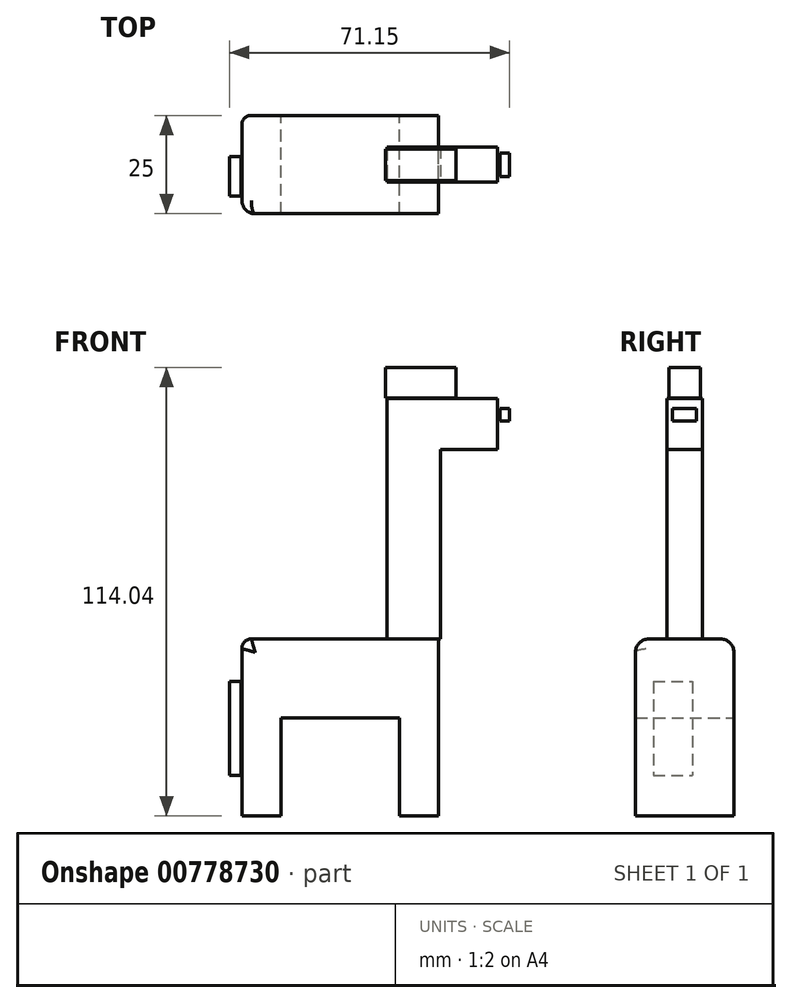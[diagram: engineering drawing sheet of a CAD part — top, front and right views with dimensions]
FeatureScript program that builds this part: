
annotation { "Feature Type Name" : "Feature", "Feature Type Description" : "" }
export const myFeature = defineFeature(function(context is Context, id is Id, definition is map)
    precondition{}
    {
        {
            var Q0;
            Q0=qCreatedBy(makeId("Front.planeOp"),FACE);
            var sketch = newSketch(context, id + "F0", { "sketchPlane" : qUnion([Q0])});
            skLineSegment(sketch, "E0.bottom", {"start": v(-30.99, 0) * mm, "end": v(-20.99, 0) * mm});
            skLineSegment(sketch, "E0.top", {"start": v(-30.99, 25) * mm, "end": v(-20.99, 25) * mm});
            skLineSegment(sketch, "E0.left", {"start": v(-30.99, 0) * mm, "end": v(-30.99, 25) * mm});
            skLineSegment(sketch, "E0.right", {"start": v(-20.99, 0) * mm, "end": v(-20.99, 25) * mm});
            skLineSegment(sketch, "E1.bottom", {"start": v(9.01, 0) * mm, "end": v(19.01, 0) * mm});
            skLineSegment(sketch, "E1.top", {"start": v(9.01, 25) * mm, "end": v(19.01, 25) * mm});
            skLineSegment(sketch, "E1.left", {"start": v(9.01, 0) * mm, "end": v(9.01, 25) * mm});
            skLineSegment(sketch, "E1.right", {"start": v(19.01, 0) * mm, "end": v(19.01, 25) * mm});
            skLineSegment(sketch, "E2.bottom", {"start": v(-30.99, 25) * mm, "end": v(19.01, 25) * mm});
            skLineSegment(sketch, "E2.top", {"start": v(-30.99, 45) * mm, "end": v(19.01, 45) * mm});
            skLineSegment(sketch, "E2.left", {"start": v(-30.99, 25) * mm, "end": v(-30.99, 45) * mm});
            skLineSegment(sketch, "E2.right", {"start": v(19.01, 25) * mm, "end": v(19.01, 45) * mm});
            skSolve(sketch);
        }
        {
            var Q0;
            Q0=makeQuery(id+"F0.imprint","IMPRINT",FACE,{"disambiguationData":[TD([[makeQuery(id+"F0.imprint","IMPRINT",EDGE,{"derivedFrom":sQuery(id+"F0.wireOp",EDGE,"E2.top")}),-1.0]])]});
            var Q1;
            Q1=makeQuery(id+"F0.imprint","IMPRINT",FACE,{"disambiguationData":[TD([[makeQuery(id+"F0.imprint","IMPRINT",EDGE,{"derivedFrom":sQuery(id+"F0.wireOp",EDGE,"E1.bottom")}),1.0]])]});
            var Q2;
            Q2=makeQuery(id+"F0.imprint","IMPRINT",FACE,{"disambiguationData":[TD([[makeQuery(id+"F0.imprint","IMPRINT",EDGE,{"derivedFrom":sQuery(id+"F0.wireOp",EDGE,"E0.bottom")}),1.0]])]});
            extrude(context, id + "F1", {"entities" : qUnion([Q0, Q1, Q2]), "endBound" : BoundingType.SYMMETRIC, "depth" : 25 * mm, "offsetDistance" : 25 * mm});
        }
        {
            var Q0;
            Q0=qCreatedBy(makeId("Front.planeOp"),FACE);
            var sketch = newSketch(context, id + "F2", { "sketchPlane" : qUnion([Q0])});
            skLineSegment(sketch, "E3.bottom", {"start": v(19.5, 45.05) * mm, "end": v(5.9, 45.05) * mm});
            skLineSegment(sketch, "E3.top", {"start": v(19.5, 93.12) * mm, "end": v(5.9, 93.12) * mm});
            skLineSegment(sketch, "E3.left", {"start": v(19.5, 45.05) * mm, "end": v(19.5, 93.12) * mm});
            skLineSegment(sketch, "E3.right", {"start": v(5.9, 45.05) * mm, "end": v(5.9, 93.12) * mm});
            skLineSegment(sketch, "E4.bottom", {"start": v(5.9, 106.11) * mm, "end": v(34.01, 106.11) * mm});
            skLineSegment(sketch, "E4.top", {"start": v(5.9, 93.12) * mm, "end": v(34.01, 93.12) * mm});
            skLineSegment(sketch, "E4.left", {"start": v(5.9, 106.11) * mm, "end": v(5.9, 93.12) * mm});
            skLineSegment(sketch, "E4.right", {"start": v(34.01, 106.11) * mm, "end": v(34.01, 93.12) * mm});
            skSolve(sketch);
        }
        {
            var Q0;
            Q0=makeQuery(id+"F2.imprint","IMPRINT",FACE,{"disambiguationData":[TD([[makeQuery(id+"F2.imprint","IMPRINT",EDGE,{"derivedFrom":sQuery(id+"F2.wireOp",EDGE,"E4.bottom")}),-1.0]])]});
            var Q1;
            Q1 = qSketchRegion(id + "F2", true);
            extrude(context, id + "F3", {"entities" : qUnion([Q0, Q1]), "endBound" : BoundingType.SYMMETRIC, "oppositeDirection" : true, "depth" : 9 * mm, "offsetDistance" : 25 * mm});
        }
        {
            var Q0;
            Q0=qCreatedBy(makeId("Front.planeOp"),FACE);
            var sketch = newSketch(context, id + "F4", { "sketchPlane" : qUnion([Q0])});
            skLineSegment(sketch, "E5.bottom", {"start": v(34.24, 99.53) * mm, "end": v(36.6, 99.53) * mm});
            skLineSegment(sketch, "E5.top", {"start": v(34.24, 96.5) * mm, "end": v(36.6, 96.5) * mm});
            skLineSegment(sketch, "E5.left", {"start": v(34.24, 99.53) * mm, "end": v(34.24, 96.5) * mm});
            skLineSegment(sketch, "E5.right", {"start": v(36.6, 99.53) * mm, "end": v(36.6, 96.5) * mm});
            skLineSegment(sketch, "E6.bottom", {"start": v(-31.55, 38.8) * mm, "end": v(-35.26, 38.8) * mm});
            skLineSegment(sketch, "E6.top", {"start": v(-31.55, 14.84) * mm, "end": v(-35.26, 14.84) * mm});
            skLineSegment(sketch, "E6.left", {"start": v(-31.55, 38.8) * mm, "end": v(-31.55, 14.84) * mm});
            skLineSegment(sketch, "E6.right", {"start": v(-35.26, 38.8) * mm, "end": v(-35.26, 14.84) * mm});
            skLineSegment(sketch, "E7.bottom", {"start": v(23.45, 106.28) * mm, "end": v(5.57, 106.28) * mm});
            skLineSegment(sketch, "E7.top", {"start": v(23.45, 114.04) * mm, "end": v(5.57, 114.04) * mm});
            skLineSegment(sketch, "E7.left", {"start": v(23.45, 106.28) * mm, "end": v(23.45, 114.04) * mm});
            skLineSegment(sketch, "E7.right", {"start": v(5.57, 106.28) * mm, "end": v(5.57, 114.04) * mm});
            skSolve(sketch);
        }
        {
            var Q0;
            Q0=makeQuery(id+"F4.imprint","IMPRINT",FACE,{"disambiguationData":[TD([[makeQuery(id+"F4.imprint","IMPRINT",EDGE,{"derivedFrom":sQuery(id+"F4.wireOp",EDGE,"E7.bottom")}),-1.0]])]});
            extrude(context, id + "F5", {"entities" : qUnion([Q0]), "endBound" : BoundingType.SYMMETRIC, "depth" : 8 * mm, "offsetDistance" : 25 * mm});
        }
        {
            var Q0;
            Q0=qCreatedBy(makeId("Front.planeOp"),FACE);
            var sketch = newSketch(context, id + "F6", { "sketchPlane" : qUnion([Q0])});
            skLineSegment(sketch, "E8.bottom", {"start": v(34.56, 99.45) * mm, "end": v(37.02, 99.45) * mm});
            skLineSegment(sketch, "E8.top", {"start": v(34.56, 96.26) * mm, "end": v(37.02, 96.26) * mm});
            skLineSegment(sketch, "E8.left", {"start": v(34.56, 99.45) * mm, "end": v(34.56, 96.26) * mm});
            skLineSegment(sketch, "E8.right", {"start": v(37.02, 99.45) * mm, "end": v(37.02, 96.26) * mm});
            skSolve(sketch);
        }
        {
            var Q0;
            Q0=makeQuery(id+"F6.imprint","IMPRINT",FACE,{"disambiguationData":[TD([[makeQuery(id+"F6.imprint","IMPRINT",EDGE,{"derivedFrom":sQuery(id+"F6.wireOp",EDGE,"E8.bottom")}),-1.0]])]});
            extrude(context, id + "F7", {"entities" : qUnion([Q0]), "endBound" : BoundingType.SYMMETRIC, "depth" : 6 * mm, "offsetDistance" : 25 * mm});
        }
        {
            var Q0;
            Q0=makeQuery(id+"F1.opExtrude","CAP_EDGE",EDGE,{"disambiguationData":[OSD([sQuery(id+"F0.wireOp",EDGE,"E2.top")])],"isStart":false});
            var Q1;
            Q1=makeQuery(id+"F1.opExtrude","CAP_EDGE",EDGE,{"disambiguationData":[OSD([sQuery(id+"F0.wireOp",EDGE,"E0.left"),sQuery(id+"F0.wireOp",EDGE,"E2.left")])],"isStart":false});
            fillet(context, id + "F8", {"entities" : qUnion([Q0, Q1]), "radius" : 3.38 * mm, "tangentPropagation" : true, "allowEdgeOverflow" : false});
        }
        {
            var Q0;
            Q0=makeQuery(id+"F1.opExtrude","CAP_EDGE",EDGE,{"disambiguationData":[OSD([sQuery(id+"F0.wireOp",EDGE,"E0.left"),sQuery(id+"F0.wireOp",EDGE,"E2.left")])],"isStart":true});
            var Q1;
            Q1=makeQuery(id+"F1.opExtrude","SWEPT_EDGE",EDGE,{"disambiguationData":[OSD([sQuery(id+"F0.wireOp",EDGE,"E2.top"),sQuery(id+"F0.wireOp",EDGE,"E2.left")])]});
            fillet(context, id + "F9", {"entities" : qUnion([Q0, Q1]), "radius" : 2.41 * mm, "tangentPropagation" : true, "allowEdgeOverflow" : false});
        }
        {
            var Q0;
            Q0=makeQuery(id+"F1.opExtrude","CAP_EDGE",EDGE,{"disambiguationData":[OSD([sQuery(id+"F0.wireOp",EDGE,"E2.top")])],"isStart":true});
            fillet(context, id + "F10", {"entities" : qUnion([Q0]), "radius" : 3.38 * mm, "tangentPropagation" : true, "allowEdgeOverflow" : false});
        }
        {
            var Q0;
            Q0=qCreatedBy(makeId("Front.planeOp"),FACE);
            var sketch = newSketch(context, id + "F11", { "sketchPlane" : qUnion([Q0])});
            skLineSegment(sketch, "E9.bottom", {"start": v(-31.6, 36.98) * mm, "end": v(-34.56, 36.98) * mm});
            skLineSegment(sketch, "E9.top", {"start": v(-31.6, 13.12) * mm, "end": v(-34.56, 13.12) * mm});
            skLineSegment(sketch, "E9.left", {"start": v(-31.6, 36.98) * mm, "end": v(-31.6, 13.12) * mm});
            skLineSegment(sketch, "E9.right", {"start": v(-34.56, 36.98) * mm, "end": v(-34.56, 13.12) * mm});
            skSolve(sketch);
        }
        {
            var Q0;
            Q0=makeQuery(id+"F11.imprint","IMPRINT",FACE,{"disambiguationData":[TD([[makeQuery(id+"F11.imprint","IMPRINT",EDGE,{"derivedFrom":sQuery(id+"F11.wireOp",EDGE,"E9.bottom")}),1.0]])]});
            extrude(context, id + "F12", {"entities" : qUnion([Q0]), "endBound" : BoundingType.SYMMETRIC, "depth" : 10 * mm, "offsetDistance" : 25 * mm});
        }
        {
            var Q0;
            Q0=makeQuery(id+"F12.opExtrude","CAP_EDGE",EDGE,{"disambiguationData":[OSD([sQuery(id+"F11.wireOp",EDGE,"E9.left")])],"isStart":false});
            cPoint(context, id + "F13", {"entities" : qUnion([Q0]), "parameter" : 0.5});
        }
        {
            var Q0;
            {var subQ0=sQuery(id+"F0.wireOp",EDGE,"E2.left");var subQ1=sQuery(id+"F0.wireOp",EDGE,"E0.left");Q0=makeQuery(id+"F8.opFillet","BLEND_EDGE",EDGE,{"blendedFrom":[makeQuery(id+"F1.opExtrude","CAP_EDGE",EDGE,{"disambiguationData":[OSD([subQ1,subQ0])],"isStart":false}),makeQuery(id+"F1.opExtrude","SWEPT_FACE",FACE,{"disambiguationData":[OSD([subQ1,subQ0])]})],"blendedInto":[makeQuery(id+"F1.opExtrude","SWEPT_FACE",FACE,{"disambiguationData":[OSD([subQ1,subQ0])]})]});}
            cPoint(context, id + "F14", {"entities" : qUnion([Q0]), "parameter" : 0.5});
        }
        {
            var Q0;
            Q0=makeQuery(id+"F12.opExtrude","SWEPT_BODY",BODY,{"disambiguationData":[OSD([sQuery(id+"F11.wireOp",EDGE,"E9.bottom"),sQuery(id+"F11.wireOp",EDGE,"E9.top"),sQuery(id+"F11.wireOp",EDGE,"E9.left"),sQuery(id+"F11.wireOp",EDGE,"E9.right")])]});
            var Q1;
            Q1 = qCreatedBy(id + "F13" ,VERTEX);
            var Q2;
            Q2 = qCreatedBy(id + "F14" ,VERTEX);
            transform(context, id + "F15", {"entities" : qUnion([Q0]), "transformType" : TransformType.TRANSLATION_DISTANCE, "transformDirection" : qUnion([Q1, Q2]), "distance" : 4.1 * mm, "makeCopy" : false});
        }
        {
            var Q0;
            Q0=qCreatedBy(makeId("Front.planeOp"),FACE);
            var sketch = newSketch(context, id + "F16", { "sketchPlane" : qUnion([Q0])});
            skCircle(sketch, "E10", {"center": v(15.87, 110.54) * mm, "radius": 1.95 * mm});
            skSolve(sketch);
        }
        {
            var Q0;
            Q0=sQuery(id+"F16.wireOp",EDGE,"E10");
            extrude(context, id + "F17", {"bodyType" : ToolBodyType.SURFACE, "surfaceEntities" : qUnion([Q0]), "endBound" : BoundingType.SYMMETRIC, "depth" : 11 * mm, "offsetDistance" : 25 * mm});
        }
        {
            var Q0;
            Q0=makeQuery(id+"F7.opExtrude","SWEPT_BODY",BODY,{"disambiguationData":[OSD([sQuery(id+"F6.wireOp",EDGE,"E8.bottom"),sQuery(id+"F6.wireOp",EDGE,"E8.top"),sQuery(id+"F6.wireOp",EDGE,"E8.left"),sQuery(id+"F6.wireOp",EDGE,"E8.right")])]});
            var Q1;
            Q1=makeQuery(id+"F7.opExtrude","CAP_VERTEX",VERTEX,{"disambiguationData":[OSD([sQuery(id+"F6.wireOp",EDGE,"E8.bottom"),sQuery(id+"F6.wireOp",EDGE,"E8.left")])],"isStart":true});
            var Q2;
            Q2=makeQuery(id+"F3.opExtrude","CAP_VERTEX",VERTEX,{"disambiguationData":[OSD([sQuery(id+"F2.wireOp",EDGE,"E4.bottom"),sQuery(id+"F2.wireOp",EDGE,"E4.right")])],"isStart":false});
            transform(context, id + "F18", {"entities" : qUnion([Q0]), "transformType" : TransformType.TRANSLATION_DISTANCE, "transformDirection" : qUnion([Q1, Q2]), "distance" : 25 * mm, "makeCopy" : false});
        }
        {
            var Q0;
            Q0=makeQuery(id+"F7.opExtrude","SWEPT_BODY",BODY,{"disambiguationData":[OSD([sQuery(id+"F6.wireOp",EDGE,"E8.bottom"),sQuery(id+"F6.wireOp",EDGE,"E8.top"),sQuery(id+"F6.wireOp",EDGE,"E8.left"),sQuery(id+"F6.wireOp",EDGE,"E8.right")])]});
            var Q1;
            Q1=makeQuery(id+"F7.opExtrude","CAP_VERTEX",VERTEX,{"disambiguationData":[OSD([sQuery(id+"F6.wireOp",EDGE,"E8.top"),sQuery(id+"F6.wireOp",EDGE,"E8.left")])],"isStart":true});
            var Q2;
            Q2=makeQuery(id+"F3.opExtrude","CAP_VERTEX",VERTEX,{"disambiguationData":[OSD([sQuery(id+"F2.wireOp",EDGE,"E4.bottom"),sQuery(id+"F2.wireOp",EDGE,"E4.right")])],"isStart":false});
            transform(context, id + "F19", {"entities" : qUnion([Q0]), "transformType" : TransformType.TRANSLATION_DISTANCE, "transformDirection" : qUnion([Q1, Q2]), "distance" : 21 * mm, "makeCopy" : false});
        }
    });
